# Revit family: L-street 40 Turbine
name_source: partatom
category: Осветительные приборы
revit_build: Autodesk Revit 2017 (Build: 20160225_1515(x64)
units: mm (PartAtom-declared; Revit-internal decimal feet)

## family parameters
Всегда вертикально = Да
Источник света = Да
На основе рабочей плоскости = Нет
Общий = Нет
При загрузке вырезать с полостями = Нет
Размер круглого соединителя = Использовать диаметр
Тип детали = Нормальный
Точка расчета площади = Нет

## types (8) — shared parameters
Видимая форма излучения при визуализации = Нет
Изготовитель = LEDEL
Излучение по длине прямоугольника = 250 мм
Излучение по ширине прямоугольника = 44 мм
Классификация нагрузок = Освещение
Комментарии к типоразмеру = Уличные
Полная установленная мощность = 33 В·А
Светофильтр = 16777215
Смещение цветовой температуры при затухании лампы = <Нет>
Угол наклона = 90.00°

## per-type parameters (varying)
| type | Артикул | Файл фотометрической сетки |
| L-street 40 Turbine 4.0K Д | 310019 | L-street 40 Turbine-33-D-4.0K-01.ies |
| L-street 40 Turbine 4.0K Ш3 | 310013 | L-street 40 Turbine-33-LLI3-4.0K-01.ies |
| L-street 40 Turbine 4.0K Ш8 | 310015 | L-Street 40 Turbine-33-LLI8-4.0K-01.ies |
| L-street 40 Turbine 4.0K Ш9 | 310025 | L-street 40 Turbine-33-LLI9-4.0K-01.ies |
| L-street 40 Turbine 5.0K Д | 310018 | L-street 40 Turbine-33-D-5.0K-01.ies |
| L-street 40 Turbine 5.0K Ш3 | 310012 | L-street 40 Turbine-33-LLI3-5.0K-01.ies |
| L-street 40 Turbine 5.0K Ш8 | 310014 | L-Street 40 Turbine-33-LLI8-5.0K01.ies |
| L-street 40 Turbine 5.0K Ш9 | 310024
310024 | L-street 40 Turbine-33-LLI9-5.0K-01.ies |
